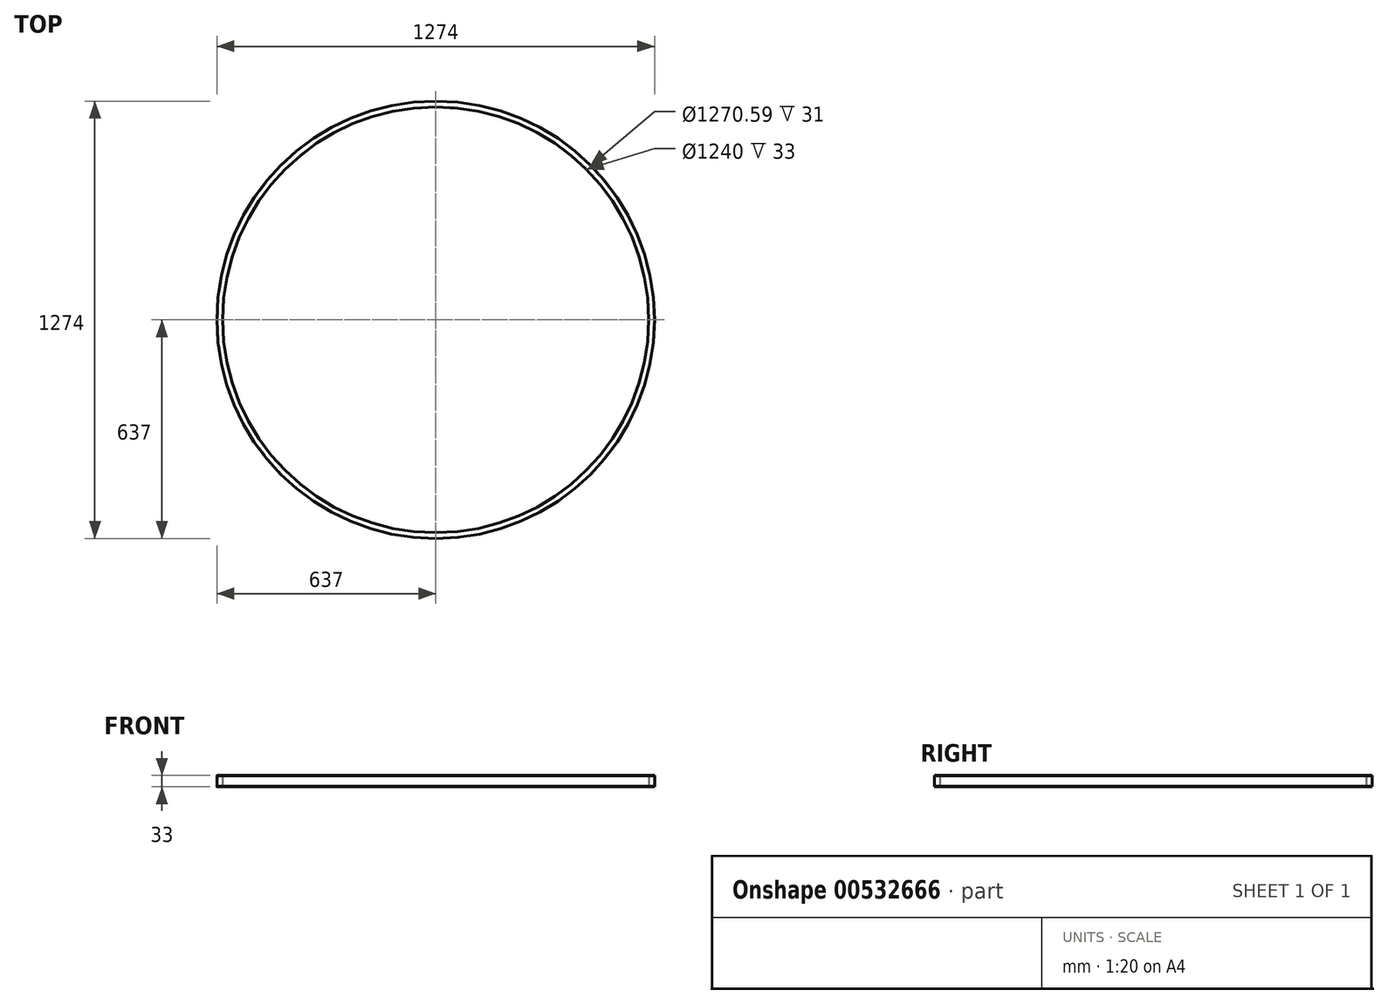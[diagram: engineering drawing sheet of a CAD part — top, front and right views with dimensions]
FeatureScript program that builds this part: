
annotation { "Feature Type Name" : "Feature", "Feature Type Description" : "" }
export const myFeature = defineFeature(function(context is Context, id is Id, definition is map)
    precondition{}
    {
        {
            var Q0;
            Q0=qCreatedBy(makeId("Front.planeOp"),FACE);
            var sketch = newSketch(context, id + "F0", { "sketchPlane" : qUnion([Q0])});
            skLineSegment(sketch, "E0", {"start": v(0, 0) * mm, "end": v(0, 14.88) * mm, "construction": true});
            skLineSegment(sketch, "E1", {"start": v(620, 0) * mm, "end": v(620, 33) * mm});
            skLineSegment(sketch, "E2", {"start": v(620, 33) * mm, "end": v(637, 33) * mm});
            skLineSegment(sketch, "E3", {"start": v(637, 33) * mm, "end": v(637, 32) * mm});
            skLineSegment(sketch, "E4", {"start": v(637, 32) * mm, "end": v(621, 32) * mm});
            skLineSegment(sketch, "E5", {"start": v(621, 32) * mm, "end": v(621, 1) * mm});
            skLineSegment(sketch, "E6", {"start": v(621, 1) * mm, "end": v(637, 1) * mm});
            skLineSegment(sketch, "E7", {"start": v(637, 1) * mm, "end": v(637, 0) * mm});
            skLineSegment(sketch, "E8", {"start": v(637, 0) * mm, "end": v(620, 0) * mm});
            skSolve(sketch);
        }
        {
            var Q0;
            Q0=makeQuery(id+"F0.imprint","IMPRINT",FACE,{"disambiguationData":[TD([[makeQuery(id+"F0.imprint","IMPRINT",EDGE,{"derivedFrom":sQuery(id+"F0.wireOp",EDGE,"E1")}),-1.0]])]});
            var Q1;
            Q1=sQuery(id+"F0.wireOp",EDGE,"E0");
            revolve(context, id + "F1", {"entities" : qUnion([Q0]), "axis" : qUnion([Q1]), "revolveType" : RevolveType.FULL});
        }
        {
            var Q0;
            Q0=qCreatedBy(makeId("Front.planeOp"),FACE);
            var sketch = newSketch(context, id + "F2", { "sketchPlane" : qUnion([Q0])});
            skLineSegment(sketch, "E9.0", {"start": v(637, 32) * mm, "end": v(-637, 32) * mm, "construction": true});
            skLineSegment(sketch, "E10", {"start": v(-637, 32) * mm, "end": v(-637, 33) * mm, "construction": true});
            skLineSegment(sketch, "E11", {"start": v(-637, 32) * mm, "end": v(-635.3, 32) * mm});
            skLineSegment(sketch, "E12.0", {"start": v(637, 1) * mm, "end": v(-637, 1) * mm, "construction": true});
            skLineSegment(sketch, "E13", {"start": v(-635.3, 32) * mm, "end": v(-635.3, 1) * mm});
            skLineSegment(sketch, "E14", {"start": v(-635.3, 1) * mm, "end": v(-637, 1) * mm});
            skLineSegment(sketch, "E15", {"start": v(-637, 1) * mm, "end": v(-637, 32) * mm});
            skLineSegment(sketch, "E16", {"start": v(0, 0) * mm, "end": v(0, 32) * mm, "construction": true});
            skSolve(sketch);
        }
        {
            var Q0;
            Q0=makeQuery(id+"F2.imprint","IMPRINT",FACE,{"disambiguationData":[TD([[makeQuery(id+"F2.imprint","IMPRINT",EDGE,{"derivedFrom":sQuery(id+"F2.wireOp",EDGE,"E13")}),-1.0]])]});
            var Q1;
            Q1=sQuery(id+"F2.wireOp",EDGE,"E15");
            var Q2;
            Q2=sQuery(id+"F2.wireOp",EDGE,"E16");
            revolve(context, id + "F3", {"entities" : qUnion([Q0]), "surfaceEntities" : qUnion([Q1]), "axis" : qUnion([Q2]), "revolveType" : RevolveType.FULL});
        }
    });
